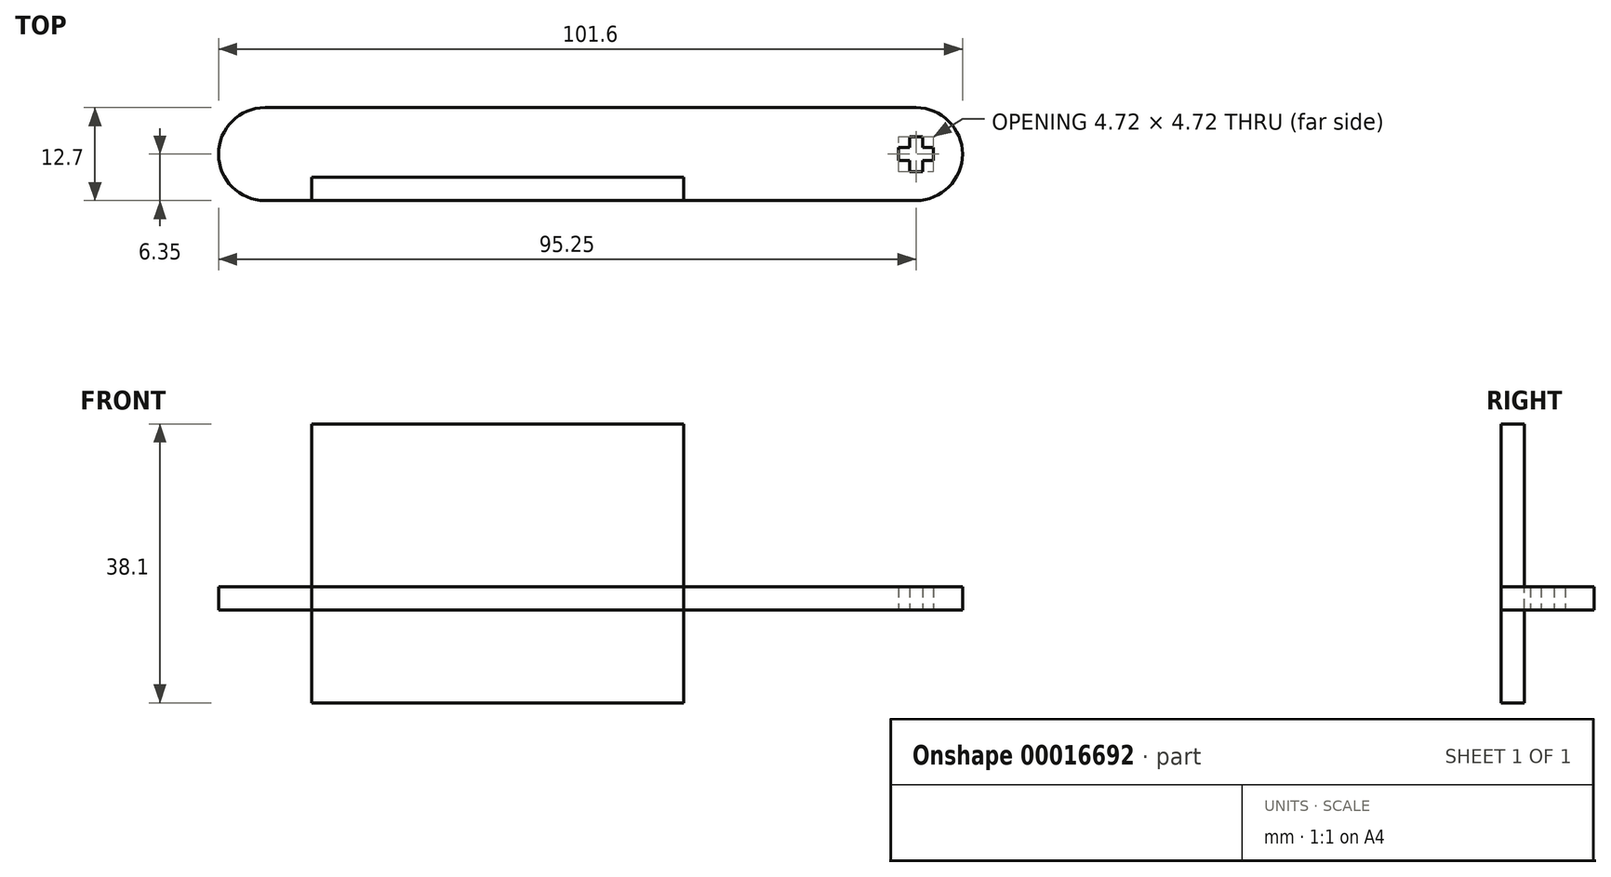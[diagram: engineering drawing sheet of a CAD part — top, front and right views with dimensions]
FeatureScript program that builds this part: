
annotation { "Feature Type Name" : "Feature", "Feature Type Description" : "" }
export const myFeature = defineFeature(function(context is Context, id is Id, definition is map)
    precondition{}
    {
        {
            var Q0;
            Q0=qCreatedBy(makeId("Top.planeOp"),FACE);
            var sketch = newSketch(context, id + "F0", { "sketchPlane" : qUnion([Q0])});
            skLineSegment(sketch, "E0.rect.bottom", {"start": v(44.45, -6.35) * mm, "end": v(-44.45, -6.35) * mm});
            skLineSegment(sketch, "E0.rect.top", {"start": v(44.45, 6.35) * mm, "end": v(-44.45, 6.35) * mm});
            skLineSegment(sketch, "E0.rect.left", {"start": v(50.8, 0) * mm, "end": v(50.8, 0) * mm});
            skLineSegment(sketch, "E0.rect.right", {"start": v(-50.8, 0) * mm, "end": v(-50.8, 0) * mm});
            skPoint(sketch, "E0.rect.middle", {"position": v(0, 0) * mm});
            skPoint(sketch, "E1.visualSharp", {"position": v(-50.8, 6.35) * mm});
            skArc(sketch, "E1.filletArc", {"start": v(-44.45, 6.35) * mm, "mid": v(-48.94, 4.5) * mm, "end": v(-50.8, 0) * mm});
            skPoint(sketch, "E2.visualSharp", {"position": v(50.8, 6.35) * mm});
            skArc(sketch, "E2.filletArc", {"start": v(50.8, 0) * mm, "mid": v(48.94, 4.5) * mm, "end": v(44.45, 6.35) * mm});
            skPoint(sketch, "E3.visualSharp", {"position": v(50.8, -6.35) * mm});
            skArc(sketch, "E3.filletArc", {"start": v(44.45, -6.35) * mm, "mid": v(48.94, -4.5) * mm, "end": v(50.8, 0) * mm});
            skPoint(sketch, "E4.visualSharp", {"position": v(-50.8, -6.35) * mm});
            skArc(sketch, "E4.filletArc", {"start": v(-50.8, 0) * mm, "mid": v(-48.94, -4.5) * mm, "end": v(-44.45, -6.35) * mm});
            skCircle(sketch, "E5", {"center": v(-44.45, 0) * mm, "radius": 0.8 * mm, "construction": true});
            skCircle(sketch, "E6", {"center": v(44.45, 0) * mm, "radius": 0.8 * mm});
            skLineSegment(sketch, "E7.rect.bottom", {"start": v(46.81, -0.89) * mm, "end": v(42.09, -0.89) * mm});
            skLineSegment(sketch, "E7.rect.top", {"start": v(46.81, 0.89) * mm, "end": v(42.09, 0.89) * mm});
            skLineSegment(sketch, "E7.rect.left", {"start": v(46.81, -0.89) * mm, "end": v(46.81, 0.89) * mm});
            skLineSegment(sketch, "E7.rect.right", {"start": v(42.09, -0.89) * mm, "end": v(42.09, 0.89) * mm});
            skLineSegment(sketch, "E8.rect.bottom", {"start": v(45.34, 2.36) * mm, "end": v(43.56, 2.36) * mm});
            skLineSegment(sketch, "E8.rect.top", {"start": v(45.34, -2.36) * mm, "end": v(43.56, -2.36) * mm});
            skLineSegment(sketch, "E8.rect.left", {"start": v(45.34, 2.36) * mm, "end": v(45.34, -2.36) * mm});
            skLineSegment(sketch, "E8.rect.right", {"start": v(43.56, 2.36) * mm, "end": v(43.56, -2.36) * mm});
            skSolve(sketch);
        }
        {
            var Q0;
            Q0=makeQuery(id+"F0.imprint","IMPRINT",FACE,{"disambiguationData":[TD([[makeQuery(id+"F0.imprint","IMPRINT",EDGE,{"derivedFrom":sQuery(id+"F0.wireOp",EDGE,"E0.rect.bottom")}),-1.0]])]});
            extrude(context, id + "F1", {"entities" : qUnion([Q0]), "depth" : 3.17 * mm});
        }
        {
            var Q0;
            Q0=makeQuery(id+"F1.opExtrude","CAP_FACE",FACE,{"disambiguationData":[OSD([sQuery(id+"F0.wireOp",EDGE,"E0.rect.bottom"),sQuery(id+"F0.wireOp",EDGE,"E0.rect.top"),sQuery(id+"F0.wireOp",EDGE,"E1.filletArc"),sQuery(id+"F0.wireOp",EDGE,"E3.filletArc"),sQuery(id+"F0.wireOp",EDGE,"E7.rect.bottom"),sQuery(id+"F0.wireOp",EDGE,"E7.rect.top"),sQuery(id+"F0.wireOp",EDGE,"E7.rect.left"),sQuery(id+"F0.wireOp",EDGE,"E7.rect.right"),sQuery(id+"F0.wireOp",EDGE,"E8.rect.bottom"),sQuery(id+"F0.wireOp",EDGE,"E8.rect.top"),sQuery(id+"F0.wireOp",EDGE,"E8.rect.left"),sQuery(id+"F0.wireOp",EDGE,"E8.rect.right")])],"isStart":false});
            var sketch = newSketch(context, id + "F2", { "sketchPlane" : qUnion([Q0])});
            skLineSegment(sketch, "E9.bottom", {"start": v(12.7, -6.35) * mm, "end": v(-38.1, -6.35) * mm});
            skLineSegment(sketch, "E9.top", {"start": v(12.7, -3.17) * mm, "end": v(-38.1, -3.18) * mm});
            skLineSegment(sketch, "E9.left", {"start": v(12.7, -6.35) * mm, "end": v(12.7, -3.17) * mm});
            skLineSegment(sketch, "E9.right", {"start": v(-38.1, -6.35) * mm, "end": v(-38.1, -3.18) * mm});
            skPoint(sketch, "E10", {"position": v(-44.45, 0) * mm});
            skArc(sketch, "E11.0", {"start": v(-44.45, 6.35) * mm, "mid": v(-50.8, 0) * mm, "end": v(-44.45, -6.35) * mm});
            skSolve(sketch);
        }
        {
            var Q0;
            Q0=makeQuery(id+"F2.imprint","IMPRINT",FACE,{"disambiguationData":[TD([[makeQuery(id+"F2.imprint","IMPRINT",EDGE,{"derivedFrom":sQuery(id+"F2.wireOp",EDGE,"E9.bottom")}),-1.0]])]});
            extrude(context, id + "F3", {"entities" : qUnion([Q0]), "operationType" : NewBodyOperationType.REMOVE, "endBound" : BoundingType.UP_TO_NEXT, "oppositeDirection" : true, "depth" : 25.4 * mm});
        }
        {
            var Q0;
            Q0=makeQuery(id+"F3.boolean.opBoolean","COPY",FACE,{"derivedFrom":makeQuery(id+"F3.opExtrude","SWEPT_FACE",FACE,{"disambiguationData":[OSD([sQuery(id+"F2.wireOp",EDGE,"E9.top")])]})});
            var sketch = newSketch(context, id + "F4", { "sketchPlane" : qUnion([Q0])});
            skLineSegment(sketch, "E12.bottom", {"start": v(-38.1, -12.7) * mm, "end": v(12.7, -12.7) * mm});
            skLineSegment(sketch, "E12.top", {"start": v(-38.1, 25.4) * mm, "end": v(12.7, 25.4) * mm});
            skLineSegment(sketch, "E12.left", {"start": v(-38.1, -12.7) * mm, "end": v(-38.1, 25.4) * mm});
            skLineSegment(sketch, "E12.right", {"start": v(12.7, -12.7) * mm, "end": v(12.7, 25.4) * mm});
            skSolve(sketch);
        }
        {
            var Q0;
            {var subQ0=sQuery(id+"F2.wireOp",EDGE,"E9.top");var subQ4=sQuery(id+"F4.wireOp",EDGE,"E12.bottom");var subQ8=makeQuery(id+"F3.boolean.opBoolean","COPY",EDGE,{"derivedFrom":makeQuery(id+"F3.opExtrude","CAP_EDGE",EDGE,{"disambiguationData":[OSD([subQ0])],"isStart":true})});var subQ9=makeQuery(id+"F4.imprint","IMPRINT",EDGE,{"derivedFrom":subQ8});var subQ10=sQuery(id+"F4.wireOp",EDGE,"E12.top");Q0=qUnion([makeQuery(id+"F4.imprint","IMPRINT",FACE,{"disambiguationData":[TD([[makeQuery(id+"F4.imprint","IMPRINT",EDGE,{"derivedFrom":subQ4}),1.0]])]}),makeQuery(id+"F4.imprint","IMPRINT",FACE,{"disambiguationData":[TD([[makeQuery(id+"F4.imprint","IMPRINT",EDGE,{"derivedFrom":subQ10}),-1.0]])]}),makeQuery(id+"F4.imprint","IMPRINT",FACE,{"disambiguationData":[TD([[subQ9,1.0]])]})]);}
            extrude(context, id + "F5", {"entities" : qUnion([Q0]), "depth" : 3.17 * mm});
        }
    });
